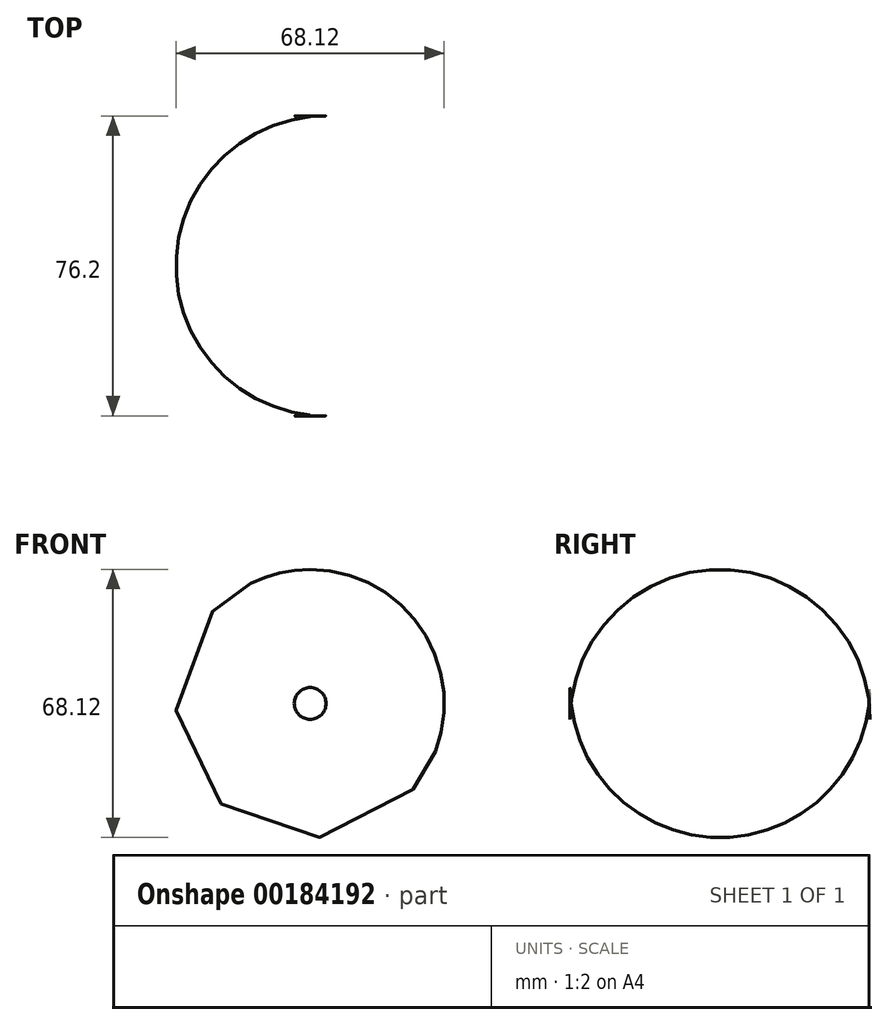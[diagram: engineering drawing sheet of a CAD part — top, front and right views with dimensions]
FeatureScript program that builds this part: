
annotation { "Feature Type Name" : "Feature", "Feature Type Description" : "" }
export const myFeature = defineFeature(function(context is Context, id is Id, definition is map)
    precondition{}
    {
        {
            var Q0;
            Q0=qCreatedBy(makeId("Front.planeOp"),FACE);
            var sketch = newSketch(context, id + "F0", { "sketchPlane" : qUnion([Q0])});
            skCircle(sketch, "E0", {"center": v(0, 0) * mm, "radius": 42.14 * mm});
            skSolve(sketch);
        }
        {
            var Q0;
            Q0=makeQuery(id+"F0.imprint","IMPRINT",FACE,{"disambiguationData":[TD([[makeQuery(id+"F0.imprint","IMPRINT",EDGE,{"derivedFrom":sQuery(id+"F0.wireOp",EDGE,"E0")}),1.0]])]});
            extrude(context, id + "F1", {"entities" : qUnion([Q0]), "depth" : 76.2 * mm});
        }
        {
            var Q0;
            Q0=makeQuery(id+"F1.opExtrude","CAP_EDGE",EDGE,{"disambiguationData":[OSD([sQuery(id+"F0.wireOp",EDGE,"E0")])],"isStart":false});
            fillet(context, id + "F2", {"entities" : qUnion([Q0]), "radius" : 38.1 * mm, "tangentPropagation" : true, "allowEdgeOverflow" : false});
        }
        {
            var Q0;
            Q0=makeQuery(id+"F1.opExtrude","SWEPT_FACE",FACE,{"disambiguationData":[OSD([sQuery(id+"F0.wireOp",EDGE,"E0")])]});
            fillet(context, id + "F3", {"entities" : qUnion([Q0]), "radius" : 38.1 * mm, "tangentPropagation" : true, "allowEdgeOverflow" : false});
        }
    });
